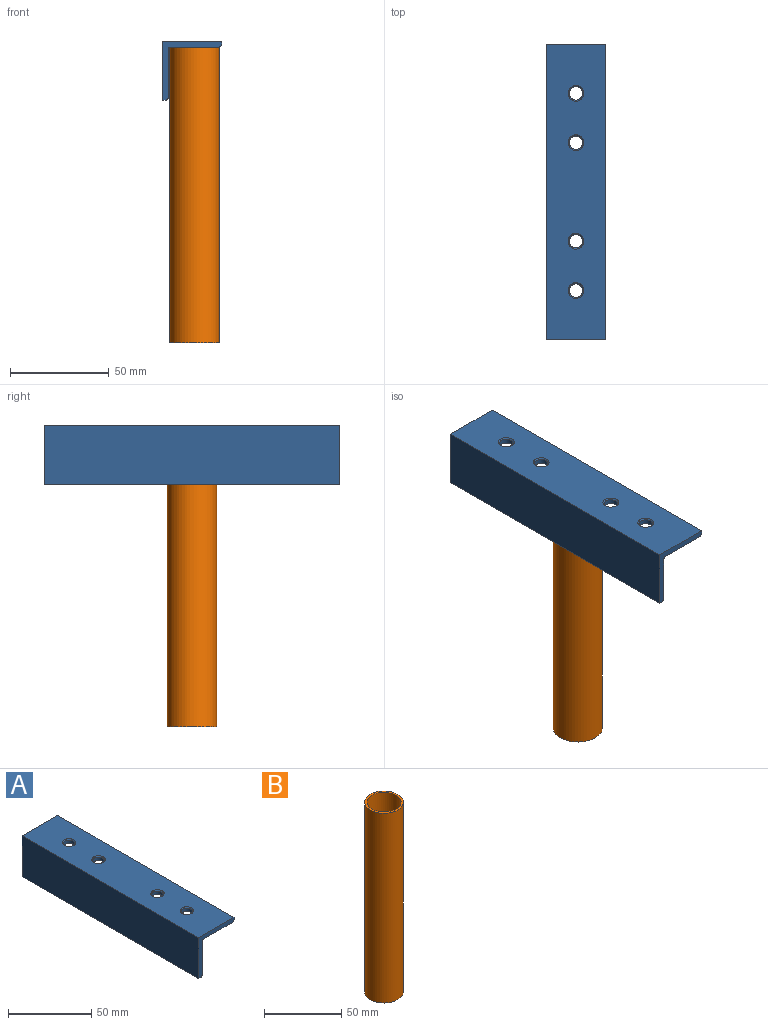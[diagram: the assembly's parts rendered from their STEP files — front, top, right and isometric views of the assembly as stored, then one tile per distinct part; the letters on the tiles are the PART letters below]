
ASSEMBLY  parts=2 mates=1
PART A: 19 faces, bbox 30x150x30 mm
  f0: plane 30x30mm, normal (0,1,0), area 170.2mm2, adj f2,f3,f4,f5,f6,f7,f8,f9
  f1: plane 30x30mm, normal (0,-1,0), area 170.2mm2, adj f2,f3,f4,f5,f6,f7,f8,f9
  f2: plane 150x30mm, normal (-1,0,0), area 4500mm2, adj f0,f1,f3,f10
  f3: plane 150x1.5mm, normal (0,0,-1), area 225mm2, adj f0,f1,f2,f4
  f4: cylinder r=1.5mm len=150mm, axis (0,-1,0), area 353.4mm2, adj f0,f1,f3,f5
  f5: plane 150x24.5mm, normal (1,0,0), area 3675mm2, adj f0,f1,f4,f6
  f6: cylinder r=1mm len=150mm, axis (0,-1,0), area 235.6mm2, adj f0,f1,f5,f7
  f7: plane 150x24.5mm, normal (0,0,-1), area 3529.7mm2, adj f0,f1,f6,f8,f11,f13,f15,f17
  f8: cylinder r=1.5mm len=150mm, axis (0,-1,0), area 353.4mm2, adj f0,f1,f7,f9
  f9: plane 150x1.5mm, normal (1,0,0), area 225mm2, adj f0,f1,f8,f10
  f10: plane 150x30mm, normal (0,0,1), area 4298.9mm2, adj f0,f1,f2,f9,f12,f14,f16,f18
  f11: cylinder r=3.4mm len=6.8mm, axis (0,0,1), area 51.3mm2, adj f7,f12
  f12: cone r=3.4mm half-angle=45deg, axis (0,0,1), area 19.7mm2, adj f10,f11
  f13: cylinder r=3.4mm len=6.8mm, axis (0,0,1), area 51.3mm2, adj f7,f14
  f14: cone r=3.4mm half-angle=45deg, axis (0,0,1), area 19.7mm2, adj f10,f13
  f15: cylinder r=3.4mm len=6.8mm, axis (0,0,1), area 51.3mm2, adj f7,f16
  f16: cone r=3.4mm half-angle=45deg, axis (0,0,1), area 19.7mm2, adj f10,f15
  f17: cylinder r=3.4mm len=6.8mm, axis (0,0,1), area 51.3mm2, adj f7,f18
  f18: cone r=3.4mm half-angle=45deg, axis (0,0,1), area 19.7mm2, adj f10,f17
PART B: 4 faces, bbox 25x25x150 mm
  f0: cylinder r=11mm len=150mm, axis (0,0,-1), area 10367.3mm2, adj f1,f2
  f1: plane 25x25mm, normal (0,0,1), area 110.7mm2, adj f0,f3
  f2: plane 25x25mm, normal (0,0,-1), area 110.7mm2, adj f0,f3
  f3: cylinder r=12.5mm len=150mm, axis (0,0,-1), area 11781mm2, adj f1,f2
PLACE A t=(-31.49,25.11,16.32)mm
PLACE B t=(-15.19,-49.89,13.32)mm
MATE fastened A.f7 <-> B.f3  axis (0,0,-1) through (-15.19,-49.89,13.32)mm
